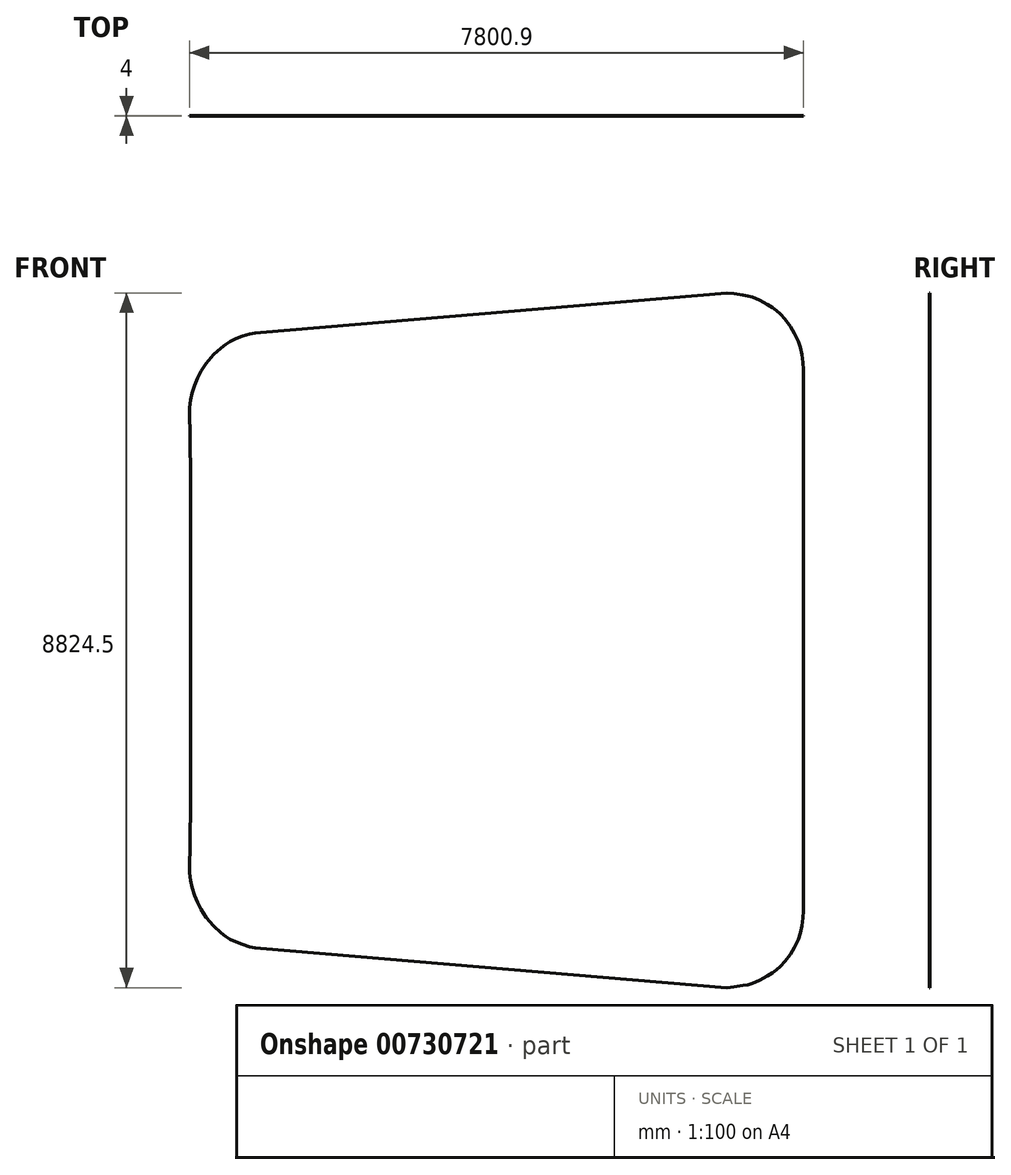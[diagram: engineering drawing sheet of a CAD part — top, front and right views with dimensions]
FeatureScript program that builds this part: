
annotation { "Feature Type Name" : "Feature", "Feature Type Description" : "" }
export const myFeature = defineFeature(function(context is Context, id is Id, definition is map)
    precondition{}
    {
        {
            var Q0;
            Q0=qCreatedBy(makeId("Front.planeOp"),FACE);
            var sketch = newSketch(context, id + "F0", { "sketchPlane" : qUnion([Q0])});
            skLineSegment(sketch, "E0", {"start": v(-3887.8, 2104.6) * mm, "end": v(-3760.8, 2104.15) * mm});
            skLineSegment(sketch, "E1", {"start": v(-3760.8, 2104.15) * mm, "end": v(-3887.8, 2104.6) * mm});
            skLineSegment(sketch, "E2", {"start": v(-3887.8, 2104.6) * mm, "end": v(-3900.45, 2956.83) * mm});
            skLineSegment(sketch, "E3", {"start": v(-3900.45, 2956.83) * mm, "end": v(-3888.82, 3049.71) * mm});
            skLineSegment(sketch, "E4", {"start": v(-3888.82, 3049.71) * mm, "end": v(-3869.26, 3141.33) * mm});
            skLineSegment(sketch, "E5", {"start": v(-3869.26, 3141.33) * mm, "end": v(-3839.16, 3238.03) * mm});
            skLineSegment(sketch, "E6", {"start": v(-3839.16, 3238.03) * mm, "end": v(-3800.55, 3331.68) * mm});
            skLineSegment(sketch, "E7", {"start": v(-3800.55, 3331.68) * mm, "end": v(-3755.54, 3418.42) * mm});
            skLineSegment(sketch, "E8", {"start": v(-3755.54, 3418.42) * mm, "end": v(-3688.41, 3518.62) * mm});
            skLineSegment(sketch, "E9", {"start": v(-3688.41, 3518.62) * mm, "end": v(-3596.26, 3627.7) * mm});
            skLineSegment(sketch, "E10", {"start": v(-3596.26, 3627.7) * mm, "end": v(-3499.33, 3714.25) * mm});
            skLineSegment(sketch, "E11", {"start": v(-3499.33, 3714.25) * mm, "end": v(-3443.68, 3758.43) * mm});
            skLineSegment(sketch, "E12", {"start": v(-3443.68, 3758.43) * mm, "end": v(-3384.83, 3797.39) * mm});
            skLineSegment(sketch, "E13", {"start": v(-3384.83, 3797.39) * mm, "end": v(-3308.5, 3833.36) * mm});
            skLineSegment(sketch, "E14", {"start": v(-3308.5, 3833.36) * mm, "end": v(-3228.75, 3862.74) * mm});
            skLineSegment(sketch, "E15", {"start": v(-3228.75, 3862.74) * mm, "end": v(-3139.87, 3891.85) * mm});
            skLineSegment(sketch, "E16", {"start": v(-3139.87, 3891.85) * mm, "end": v(-3070.2, 3905.24) * mm});
            skLineSegment(sketch, "E17", {"start": v(-3070.2, 3905.24) * mm, "end": v(-2999.36, 3910.4) * mm});
            skLineSegment(sketch, "E18", {"start": v(-2999.36, 3910.4) * mm, "end": v(2924.63, 4412.25) * mm});
            skLineSegment(sketch, "E19", {"start": v(2924.63, 4412.25) * mm, "end": v(3018.1, 4402.32) * mm});
            skLineSegment(sketch, "E20", {"start": v(3018.1, 4402.32) * mm, "end": v(3129.97, 4384.08) * mm});
            skLineSegment(sketch, "E21", {"start": v(3129.97, 4384.08) * mm, "end": v(3189.8, 4374.32) * mm});
            skLineSegment(sketch, "E22", {"start": v(3189.8, 4374.32) * mm, "end": v(3248.46, 4360.4) * mm});
            skLineSegment(sketch, "E23", {"start": v(3248.46, 4360.4) * mm, "end": v(3338.88, 4321.57) * mm});
            skLineSegment(sketch, "E24", {"start": v(3338.88, 4321.57) * mm, "end": v(3442.3, 4265.23) * mm});
            skLineSegment(sketch, "E25", {"start": v(3442.3, 4265.23) * mm, "end": v(3504.87, 4226.52) * mm});
            skLineSegment(sketch, "E26", {"start": v(3504.87, 4226.52) * mm, "end": v(3556.89, 4187.96) * mm});
            skLineSegment(sketch, "E27", {"start": v(3556.89, 4187.96) * mm, "end": v(3604.72, 4144.5) * mm});
            skLineSegment(sketch, "E28", {"start": v(3604.72, 4144.5) * mm, "end": v(3661.59, 4080.37) * mm});
            skLineSegment(sketch, "E29", {"start": v(3661.59, 4080.37) * mm, "end": v(3733.44, 3987.03) * mm});
            skLineSegment(sketch, "E30", {"start": v(3733.44, 3987.03) * mm, "end": v(3784.88, 3897.52) * mm});
            skLineSegment(sketch, "E31", {"start": v(3784.88, 3897.52) * mm, "end": v(3836.34, 3795.74) * mm});
            skLineSegment(sketch, "E32", {"start": v(3836.34, 3795.74) * mm, "end": v(3860.85, 3716.62) * mm});
            skLineSegment(sketch, "E33", {"start": v(3860.85, 3716.62) * mm, "end": v(3876.8, 3629.4) * mm});
            skLineSegment(sketch, "E34", {"start": v(3876.8, 3629.4) * mm, "end": v(3891.03, 3528.12) * mm});
            skLineSegment(sketch, "E35", {"start": v(3891.03, 3528.12) * mm, "end": v(3900.45, 3438.54) * mm});
            skLineSegment(sketch, "E36", {"start": v(3900.45, 3438.54) * mm, "end": v(3900.45, 2802.2) * mm});
            skLineSegment(sketch, "E37", {"start": v(3900.45, 2802.2) * mm, "end": v(3773.45, 2802.2) * mm});
            skLineSegment(sketch, "E38", {"start": v(3773.45, 2802.2) * mm, "end": v(3900.45, 2802.2) * mm});
            skLineSegment(sketch, "E39", {"start": v(3900.45, 2802.2) * mm, "end": v(3900.45, 2320.68) * mm});
            skLineSegment(sketch, "E40", {"start": v(3900.45, 2320.68) * mm, "end": v(3773.45, 2320.68) * mm});
            skLineSegment(sketch, "E41", {"start": v(3773.45, 2320.68) * mm, "end": v(3900.45, 2320.68) * mm});
            skLineSegment(sketch, "E42", {"start": v(3900.45, 2320.68) * mm, "end": v(3900.45, 0.01) * mm});
            skLineSegment(sketch, "E43", {"start": v(3900.45, 0.01) * mm, "end": v(3773.45, 0.01) * mm});
            skLineSegment(sketch, "E44", {"start": v(3773.45, 0.01) * mm, "end": v(3900.45, 0.01) * mm});
            skLineSegment(sketch, "E45", {"start": v(3900.45, 0.01) * mm, "end": v(3900.45, -2320.66) * mm});
            skLineSegment(sketch, "E46", {"start": v(3900.45, -2320.66) * mm, "end": v(3773.45, -2320.66) * mm});
            skLineSegment(sketch, "E47", {"start": v(3773.45, -2320.66) * mm, "end": v(3900.45, -2320.66) * mm});
            skLineSegment(sketch, "E48", {"start": v(3900.45, -2320.66) * mm, "end": v(3900.45, -2802.17) * mm});
            skLineSegment(sketch, "E49", {"start": v(3900.45, -2802.17) * mm, "end": v(3773.45, -2802.17) * mm});
            skLineSegment(sketch, "E50", {"start": v(3773.45, -2802.17) * mm, "end": v(3900.45, -2802.17) * mm});
            skLineSegment(sketch, "E51", {"start": v(3900.45, -2802.17) * mm, "end": v(3900.45, -3438.51) * mm});
            skLineSegment(sketch, "E52", {"start": v(3900.45, -3438.51) * mm, "end": v(3891.03, -3528.1) * mm});
            skLineSegment(sketch, "E53", {"start": v(3891.03, -3528.1) * mm, "end": v(3876.8, -3629.4) * mm});
            skLineSegment(sketch, "E54", {"start": v(3876.8, -3629.4) * mm, "end": v(3860.85, -3716.6) * mm});
            skLineSegment(sketch, "E55", {"start": v(3860.85, -3716.6) * mm, "end": v(3836.34, -3795.71) * mm});
            skLineSegment(sketch, "E56", {"start": v(3836.34, -3795.71) * mm, "end": v(3784.88, -3897.5) * mm});
            skLineSegment(sketch, "E57", {"start": v(3784.88, -3897.5) * mm, "end": v(3733.44, -3987) * mm});
            skLineSegment(sketch, "E58", {"start": v(3733.44, -3987) * mm, "end": v(3661.59, -4080.34) * mm});
            skLineSegment(sketch, "E59", {"start": v(3661.59, -4080.34) * mm, "end": v(3604.72, -4144.48) * mm});
            skLineSegment(sketch, "E60", {"start": v(3604.72, -4144.48) * mm, "end": v(3556.89, -4187.96) * mm});
            skLineSegment(sketch, "E61", {"start": v(3556.89, -4187.96) * mm, "end": v(3504.87, -4226.5) * mm});
            skLineSegment(sketch, "E62", {"start": v(3504.87, -4226.5) * mm, "end": v(3442.3, -4265.2) * mm});
            skLineSegment(sketch, "E63", {"start": v(3442.3, -4265.2) * mm, "end": v(3338.88, -4321.54) * mm});
            skLineSegment(sketch, "E64", {"start": v(3338.88, -4321.54) * mm, "end": v(3248.46, -4360.4) * mm});
            skLineSegment(sketch, "E65", {"start": v(3248.46, -4360.4) * mm, "end": v(3189.8, -4374.32) * mm});
            skLineSegment(sketch, "E66", {"start": v(3189.8, -4374.32) * mm, "end": v(3129.97, -4384.05) * mm});
            skLineSegment(sketch, "E67", {"start": v(3129.97, -4384.05) * mm, "end": v(3018.1, -4402.29) * mm});
            skLineSegment(sketch, "E68", {"start": v(3018.1, -4402.29) * mm, "end": v(2924.63, -4412.25) * mm});
            skLineSegment(sketch, "E69", {"start": v(2924.63, -4412.25) * mm, "end": v(-2999.36, -3910.4) * mm});
            skLineSegment(sketch, "E70", {"start": v(-2999.36, -3910.4) * mm, "end": v(-3070.2, -3905.21) * mm});
            skLineSegment(sketch, "E71", {"start": v(-3070.2, -3905.21) * mm, "end": v(-3139.87, -3891.85) * mm});
            skLineSegment(sketch, "E72", {"start": v(-3139.87, -3891.85) * mm, "end": v(-3228.75, -3862.72) * mm});
            skLineSegment(sketch, "E73", {"start": v(-3228.75, -3862.72) * mm, "end": v(-3308.5, -3833.33) * mm});
            skLineSegment(sketch, "E74", {"start": v(-3308.5, -3833.33) * mm, "end": v(-3384.83, -3797.36) * mm});
            skLineSegment(sketch, "E75", {"start": v(-3384.83, -3797.36) * mm, "end": v(-3443.68, -3758.4) * mm});
            skLineSegment(sketch, "E76", {"start": v(-3443.68, -3758.4) * mm, "end": v(-3499.33, -3714.23) * mm});
            skLineSegment(sketch, "E77", {"start": v(-3499.33, -3714.23) * mm, "end": v(-3596.26, -3627.7) * mm});
            skLineSegment(sketch, "E78", {"start": v(-3596.26, -3627.7) * mm, "end": v(-3688.41, -3518.6) * mm});
            skLineSegment(sketch, "E79", {"start": v(-3688.41, -3518.6) * mm, "end": v(-3755.54, -3418.4) * mm});
            skLineSegment(sketch, "E80", {"start": v(-3755.54, -3418.4) * mm, "end": v(-3800.55, -3331.65) * mm});
            skLineSegment(sketch, "E81", {"start": v(-3800.55, -3331.65) * mm, "end": v(-3839.16, -3238) * mm});
            skLineSegment(sketch, "E82", {"start": v(-3839.16, -3238) * mm, "end": v(-3869.26, -3141.3) * mm});
            skLineSegment(sketch, "E83", {"start": v(-3869.26, -3141.3) * mm, "end": v(-3888.82, -3049.71) * mm});
            skLineSegment(sketch, "E84", {"start": v(-3888.82, -3049.71) * mm, "end": v(-3900.45, -2956.83) * mm});
            skLineSegment(sketch, "E85", {"start": v(-3900.45, -2956.83) * mm, "end": v(-3887.8, -2104.58) * mm});
            skLineSegment(sketch, "E86", {"start": v(-3887.8, -2104.58) * mm, "end": v(-3760.8, -2106.49) * mm});
            skLineSegment(sketch, "E87", {"start": v(-3760.8, -2106.49) * mm, "end": v(-3887.8, -2104.58) * mm});
            skLineSegment(sketch, "E88", {"start": v(-3887.8, -2104.58) * mm, "end": v(-3889.55, -1615.43) * mm});
            skLineSegment(sketch, "E89", {"start": v(-3889.55, -1615.43) * mm, "end": v(-3762.55, -1614.97) * mm});
            skLineSegment(sketch, "E90", {"start": v(-3762.55, -1614.97) * mm, "end": v(-3889.55, -1615.43) * mm});
            skLineSegment(sketch, "E91", {"start": v(-3889.55, -1615.43) * mm, "end": v(-3889.55, 0.01) * mm});
            skLineSegment(sketch, "E92", {"start": v(-3889.55, 0.01) * mm, "end": v(-3762.55, 0.01) * mm});
            skLineSegment(sketch, "E93", {"start": v(-3762.55, 0.01) * mm, "end": v(-3889.55, 0.01) * mm});
            skLineSegment(sketch, "E94", {"start": v(-3889.55, 0.01) * mm, "end": v(-3889.55, 1615.45) * mm});
            skLineSegment(sketch, "E95", {"start": v(-3889.55, 1615.45) * mm, "end": v(-3762.55, 1615.45) * mm});
            skLineSegment(sketch, "E96", {"start": v(-3762.55, 1615.45) * mm, "end": v(-3889.55, 1615.45) * mm});
            skLineSegment(sketch, "E97", {"start": v(-3889.55, 1615.45) * mm, "end": v(-3887.8, 2104.6) * mm});
            skSolve(sketch);
        }
        {
            var Q0;
            Q0 = qSketchRegion(id + "F0", true);
            extrude(context, id + "F1", {"entities" : qUnion([Q0]), "depth" : 4 * mm, "offsetDistance" : 25 * mm});
        }
    });
